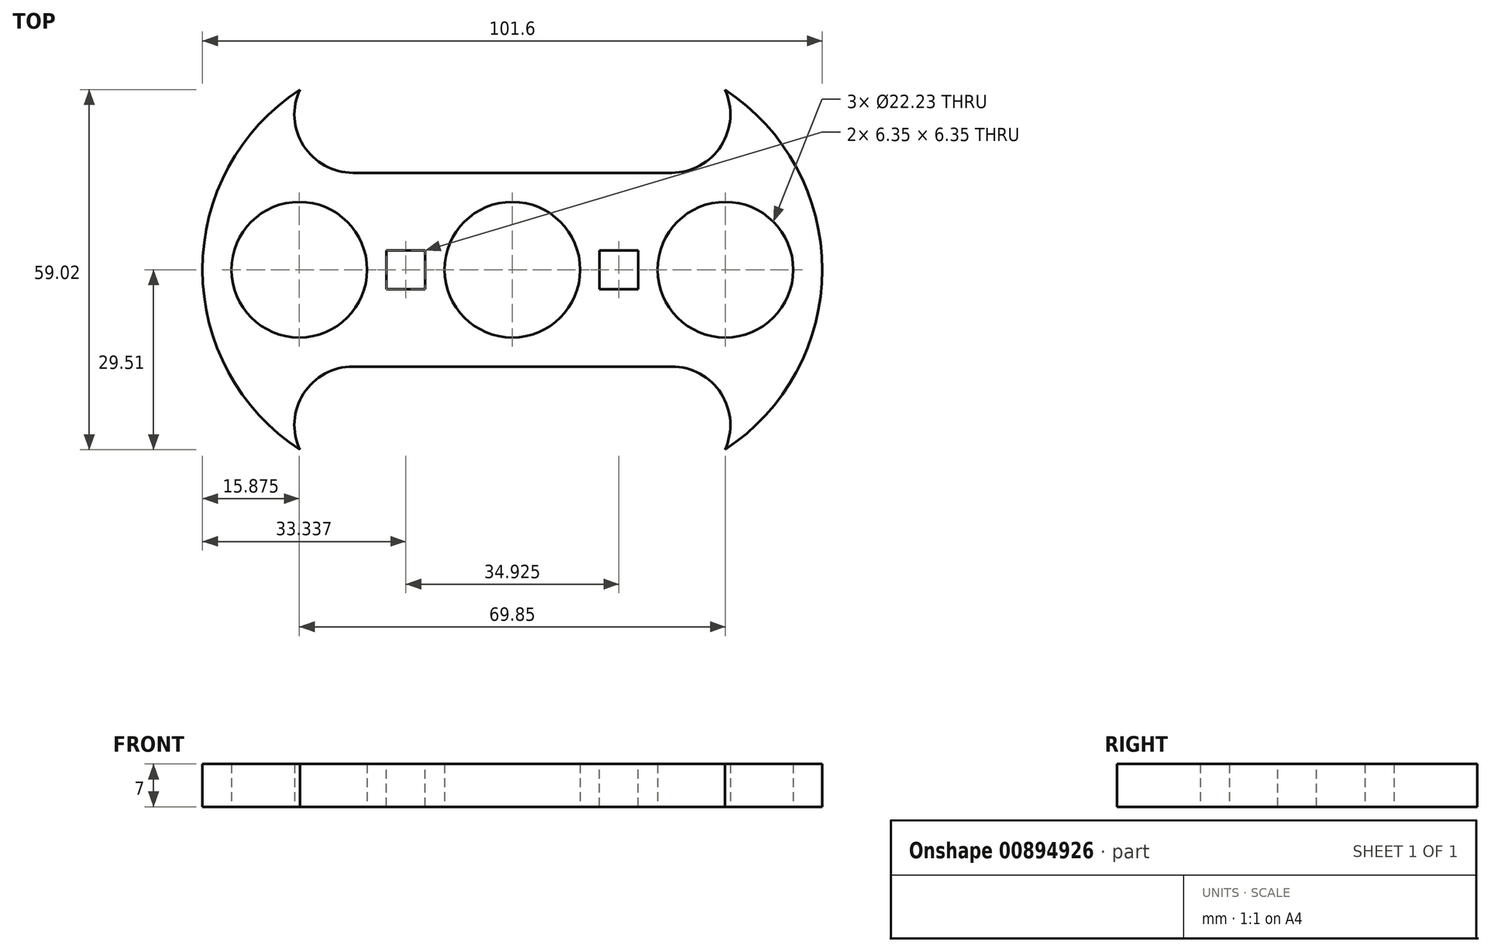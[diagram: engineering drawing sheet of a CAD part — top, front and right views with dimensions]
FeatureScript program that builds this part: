
annotation { "Feature Type Name" : "Feature", "Feature Type Description" : "" }
export const myFeature = defineFeature(function(context is Context, id is Id, definition is map)
    precondition{}
    {
        {
            var Q0;
            Q0=qCreatedBy(makeId("Top.planeOp"),FACE);
            var sketch = newSketch(context, id + "F0", { "sketchPlane" : qUnion([Q0])});
            skLineSegment(sketch, "E0.bottom", {"start": v(-34.92, -15.87) * mm, "end": v(34.93, -15.87) * mm});
            skLineSegment(sketch, "E0.top", {"start": v(-26.14, 15.87) * mm, "end": v(34.93, 15.87) * mm});
            skLineSegment(sketch, "E0.left", {"start": v(-50.8, 0) * mm, "end": v(-50.8, 0) * mm});
            skLineSegment(sketch, "E0.right", {"start": v(50.8, 0) * mm, "end": v(50.8, 0) * mm});
            skPoint(sketch, "E0.middle", {"position": v(0, 0) * mm});
            skCircle(sketch, "E1", {"center": v(0, 0) * mm, "radius": 11.11 * mm});
            skCircle(sketch, "E2", {"center": v(-34.92, 0) * mm, "radius": 11.11 * mm});
            skCircle(sketch, "E3", {"center": v(34.93, 0) * mm, "radius": 11.11 * mm});
            skPoint(sketch, "E4.visualSharp", {"position": v(-50.8, 15.87) * mm});
            skPoint(sketch, "E5.visualSharp", {"position": v(-50.8, -15.87) * mm});
            skArc(sketch, "E5.filletArc", {"start": v(-50.8, 0) * mm, "mid": v(-46.15, -11.23) * mm, "end": v(-34.92, -15.87) * mm});
            skPoint(sketch, "E6.visualSharp", {"position": v(50.8, 15.87) * mm});
            skArc(sketch, "E6.filletArc", {"start": v(50.8, 0) * mm, "mid": v(46.15, 11.23) * mm, "end": v(34.93, 15.87) * mm});
            skPoint(sketch, "E7.visualSharp", {"position": v(50.8, -15.87) * mm});
            skArc(sketch, "E7.filletArc", {"start": v(34.93, -15.87) * mm, "mid": v(46.15, -11.23) * mm, "end": v(50.8, 0) * mm});
            skArc(sketch, "E8", {"start": v(-50.8, 0) * mm, "mid": v(-46.55, 16.78) * mm, "end": v(-34.84, 29.51) * mm});
            skArc(sketch, "E9", {"start": v(-26.14, 15.87) * mm, "mid": v(-34.22, 20.3) * mm, "end": v(-34.84, 29.51) * mm});
            skArc(sketch, "E10.MirrorCS", {"start": v(50.8, 0) * mm, "mid": v(46.55, 16.78) * mm, "end": v(34.84, 29.51) * mm});
            skArc(sketch, "E11.MirrorCS", {"start": v(26.14, 15.87) * mm, "mid": v(34.22, 20.3) * mm, "end": v(34.84, 29.51) * mm});
            skArc(sketch, "E12.MirrorCS", {"start": v(-50.8, 0) * mm, "mid": v(-46.55, -16.78) * mm, "end": v(-34.84, -29.51) * mm});
            skArc(sketch, "E13.MirrorCS", {"start": v(-26.14, -15.87) * mm, "mid": v(-34.22, -20.3) * mm, "end": v(-34.84, -29.51) * mm});
            skArc(sketch, "E14.MirrorCS", {"start": v(26.14, -15.87) * mm, "mid": v(34.22, -20.3) * mm, "end": v(34.84, -29.51) * mm});
            skArc(sketch, "E15.MirrorCS", {"start": v(50.8, 0) * mm, "mid": v(46.55, -16.78) * mm, "end": v(34.84, -29.51) * mm});
            skSolve(sketch);
        }
        {
            var Q0;
            Q0 = qSketchRegion(id + "F0", true);
            extrude(context, id + "F1", {"entities" : qUnion([Q0]), "depth" : 7 * mm, "offsetDistance" : 25.4 * mm});
        }
        {
            var Q0;
            Q0=makeQuery(id+"F1.opExtrude","CAP_FACE",FACE,{"disambiguationData":[OSD([sQuery(id+"F0.wireOp",EDGE,"E0.bottom"),sQuery(id+"F0.wireOp",EDGE,"E0.top"),sQuery(id+"F0.wireOp",EDGE,"E1"),sQuery(id+"F0.wireOp",EDGE,"E2"),sQuery(id+"F0.wireOp",EDGE,"E3"),sQuery(id+"F0.wireOp",EDGE,"E8"),sQuery(id+"F0.wireOp",EDGE,"E9"),sQuery(id+"F0.wireOp",EDGE,"E10.MirrorCS"),sQuery(id+"F0.wireOp",EDGE,"E11.MirrorCS"),sQuery(id+"F0.wireOp",EDGE,"E12.MirrorCS"),sQuery(id+"F0.wireOp",EDGE,"E13.MirrorCS"),sQuery(id+"F0.wireOp",EDGE,"E14.MirrorCS"),sQuery(id+"F0.wireOp",EDGE,"E15.MirrorCS")])],"isStart":false});
            var sketch = newSketch(context, id + "F2", { "sketchPlane" : qUnion([Q0])});
            skLineSegment(sketch, "E16.bottom", {"start": v(20.64, 3.18) * mm, "end": v(14.29, 3.18) * mm});
            skLineSegment(sketch, "E16.top", {"start": v(20.64, -3.17) * mm, "end": v(14.29, -3.17) * mm});
            skLineSegment(sketch, "E16.left", {"start": v(20.64, 3.18) * mm, "end": v(20.64, -3.18) * mm});
            skLineSegment(sketch, "E16.right", {"start": v(14.29, 3.18) * mm, "end": v(14.29, -3.17) * mm});
            skPoint(sketch, "E16.middle", {"position": v(17.46, 0) * mm});
            skLineSegment(sketch, "E17.MirrorCS", {"start": v(-20.64, -3.17) * mm, "end": v(-14.29, -3.17) * mm});
            skLineSegment(sketch, "E18.MirrorCS", {"start": v(-14.29, 3.18) * mm, "end": v(-14.29, -3.17) * mm});
            skLineSegment(sketch, "E19.MirrorCS", {"start": v(-20.64, 3.18) * mm, "end": v(-14.29, 3.18) * mm});
            skLineSegment(sketch, "E20.MirrorCS", {"start": v(-20.64, 3.18) * mm, "end": v(-20.64, -3.18) * mm});
            skSolve(sketch);
        }
        {
            var Q0;
            Q0 = qSketchRegion(id + "F2", true);
            extrude(context, id + "F3", {"entities" : qUnion([Q0]), "operationType" : NewBodyOperationType.REMOVE, "endBound" : BoundingType.UP_TO_NEXT, "oppositeDirection" : true, "depth" : 25.4 * mm, "offsetDistance" : 25.4 * mm});
        }
    });
